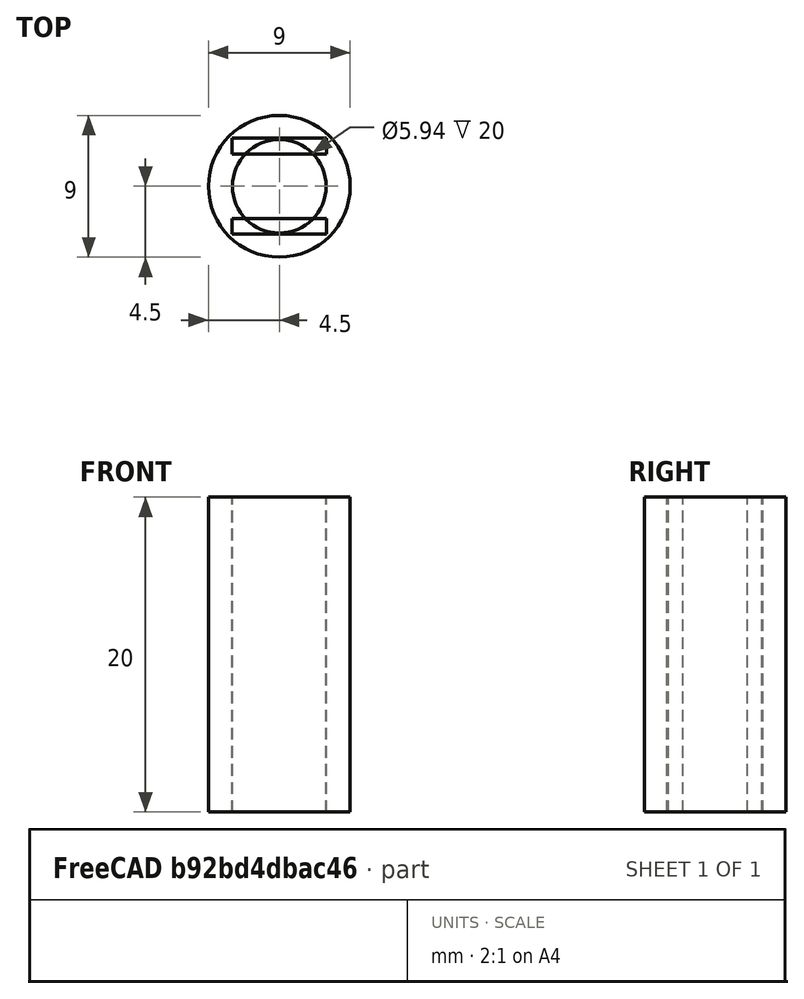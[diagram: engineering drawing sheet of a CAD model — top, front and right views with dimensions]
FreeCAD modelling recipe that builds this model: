
FCSTD DOCUMENT  (FreeCAD 0.17R13522 (Git))
Label: enganche
License: All rights reserved
LicenseURL: http://en.wikipedia.org/wiki/All_rights_reserved
objects: Part::Cylinder×2, Part::Box×2, Part::Cut×1, App::MeasureDistance×1
note: 5 computed .brp shape members not serialized (recipe doc carries the construction recipe); baked Part::Feature solids carry a one-line shape summary decoded from their .brp

FEATURE [Part::Cylinder] Cylinder  label="Cilindro"
  Angle = 360
  AttacherType = Attacher::AttachEngine3D
  Height = 20
  Radius = 4.5
FEATURE [Part::Cylinder] Cylinder001  label="Cilindro001"
  Angle = 360
  AttacherType = Attacher::AttachEngine3D
  Height = 20
  Radius = 2.97
FEATURE [Part::Box] Box  label="Cubo"
  AttacherType = Attacher::AttachEngine3D
  Height = 20
  Length = 6
  Placement = pos=(-3,2.05,0) rot=(0,0,1;0rad)
  Width = 1
FEATURE [Part::Box] Box001  label="Cubo001"
  AttacherType = Attacher::AttachEngine3D
  Height = 20
  Length = 6
  Placement = pos=(-3,-3.05,0) rot=(0,0,1;0rad)
  Width = 1
FEATURE [Part::Cut] Cut
  Base = -> Cylinder
  Tool = -> Cylinder001
FEATURE [App::MeasureDistance] Distance  label="Distance: 4,71 mm"
  Distance = 4.71007
  P1 = (-0.138287,2.3,10)
  P2 = (0.177104,-2.3995,10)
